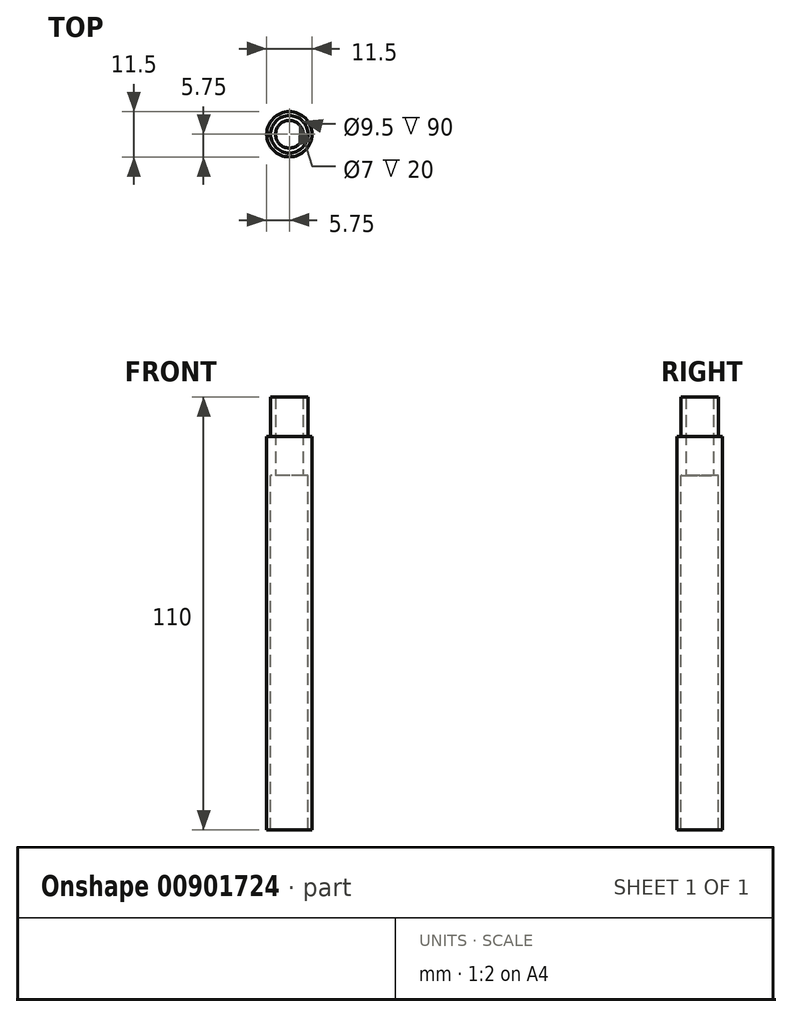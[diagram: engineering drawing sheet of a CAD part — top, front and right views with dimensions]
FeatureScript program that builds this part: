
annotation { "Feature Type Name" : "Feature", "Feature Type Description" : "" }
export const myFeature = defineFeature(function(context is Context, id is Id, definition is map)
    precondition{}
    {
        {
            var Q0;
            Q0=qCreatedBy(makeId("Top.planeOp"),FACE);
            var sketch = newSketch(context, id + "F0", { "sketchPlane" : qUnion([Q0])});
            skCircle(sketch, "E0", {"center": v(0, 0) * mm, "radius": 4.75 * mm});
            skCircle(sketch, "E1", {"center": v(0, 0) * mm, "radius": 5.75 * mm});
            skSolve(sketch);
        }
        {
            var Q0;
            Q0=makeQuery(id+"F0.imprint","IMPRINT",FACE,{"disambiguationData":[TD([[makeQuery(id+"F0.imprint","IMPRINT",EDGE,{"derivedFrom":sQuery(id+"F0.wireOp",EDGE,"E0")}),-1.0]])]});
            extrude(context, id + "F1", {"entities" : qUnion([Q0]), "oppositeDirection" : true, "depth" : 100 * mm, "offsetDistance" : 25 * mm});
        }
        {
            var Q0;
            Q0=makeQuery(id+"F1.opExtrude","CAP_FACE",FACE,{"disambiguationData":[OSD([sQuery(id+"F0.wireOp",EDGE,"E0"),sQuery(id+"F0.wireOp",EDGE,"E1")])],"isStart":true});
            var sketch = newSketch(context, id + "F2", { "sketchPlane" : qUnion([Q0])});
            skCircle(sketch, "E2", {"center": v(0, 0) * mm, "radius": 4.76 * mm});
            skCircle(sketch, "E3", {"center": v(0, 0) * mm, "radius": 3.5 * mm});
            skSolve(sketch);
        }
        {
            var Q0;
            Q0=makeQuery(id+"F2.imprint","IMPRINT",FACE,{"disambiguationData":[TD([[makeQuery(id+"F2.imprint","IMPRINT",EDGE,{"derivedFrom":sQuery(id+"F2.wireOp",EDGE,"E3")}),-1.0]])]});
            extrude(context, id + "F3", {"entities" : qUnion([Q0]), "operationType" : NewBodyOperationType.ADD, "depth" : 10 * mm, "offsetDistance" : 25 * mm, "hasSecondDirection" : true, "secondDirectionOppositeDirection" : true, "secondDirectionDepth" : 10 * mm});
        }
    });
